# Revit family: UHNP115-SS01B
name_source: partatom
category: Specialty Equipment
revit_build: Autodesk Revit 2017 (Build: 20160225_1515(x64)
units: mm (PartAtom-declared; Revit-internal decimal feet)

## family parameters
Always vertical = Yes
Cut with Voids When Loaded = No
Part Type = Normal
Room Calculation Point = No
Round Connector Dimension = Use Diameter
Shared = No
Work Plane-Based = No

## types (1)
- UHNP115-SS01B
    Depth = 22 15/16"
    Description = 15" Nugget Ice
    Door Swing = Field Reversible
    Features and specifications = Makes cylindrical compressed ice bits approx. 3⁄4” L x 1⁄2” H
    Finish = Stainless Solid
    Height = 33 11/16"
    Lock = No
    Manufacturer = U-LINE
    Model = UHNP115-SS01B
    Pump = Yes
    Temperature range = Produces up to 90 lb of ice per day
    U-Adjust interior = Eco friendly - most efficient type of specialty ice
    URL = https://www.yepsketch.com
    Voltage/Hz = 115 v / 60 hz
    Width = 14 15/16"
    shipping weight = 106 lb

## geometry (parser evidence)
native form markers: Sweep x2
no freeform markers — native parametric forms only
